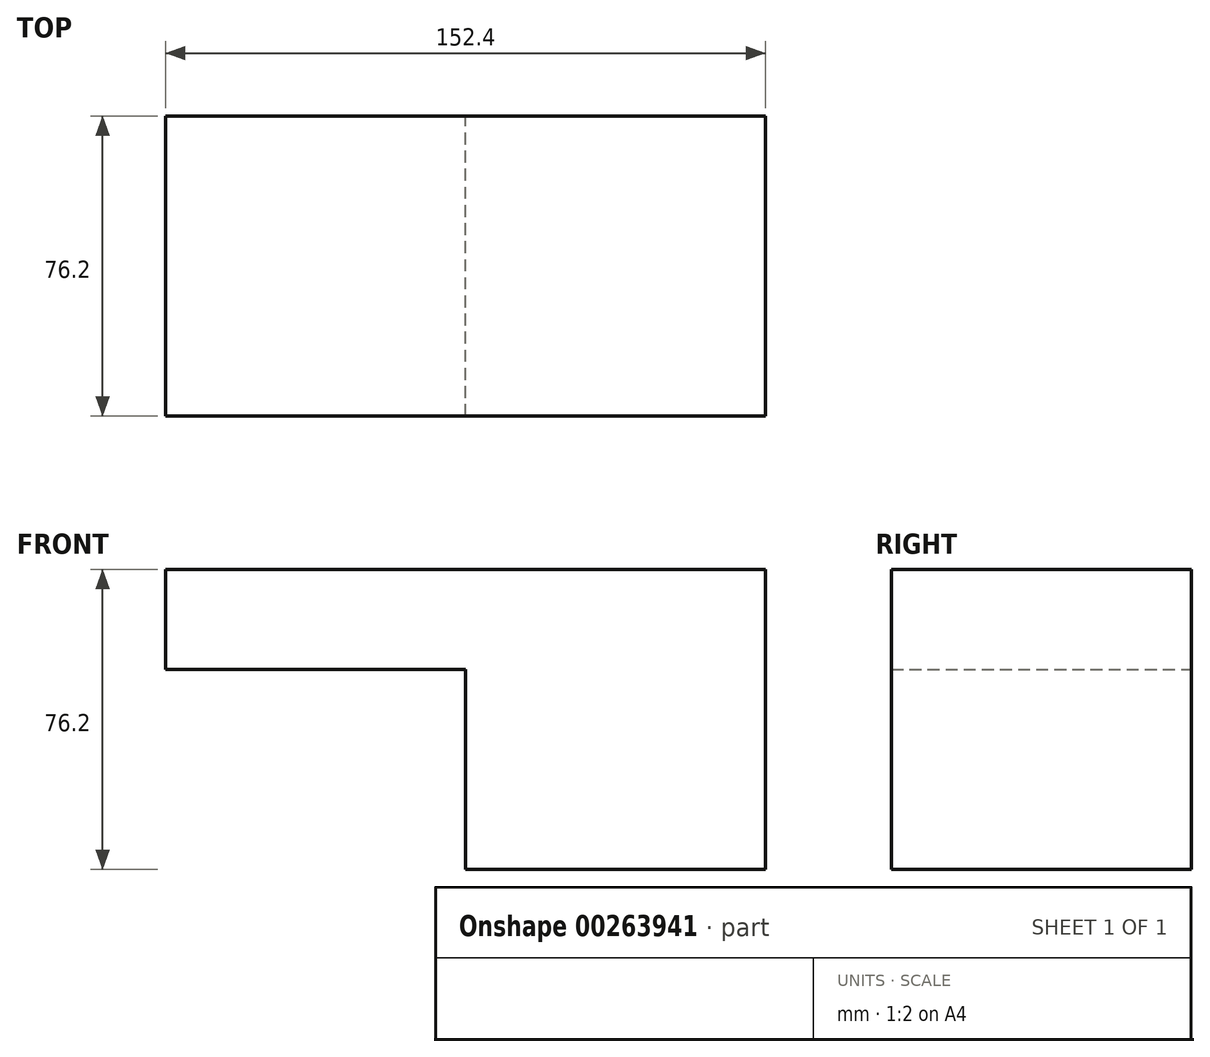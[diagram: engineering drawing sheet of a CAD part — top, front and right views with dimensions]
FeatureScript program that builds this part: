
annotation { "Feature Type Name" : "Feature", "Feature Type Description" : "" }
export const myFeature = defineFeature(function(context is Context, id is Id, definition is map)
    precondition{}
    {
        {
            var Q0;
            Q0=qCreatedBy(makeId("Top.planeOp"),FACE);
            var sketch = newSketch(context, id + "F0", { "sketchPlane" : qUnion([Q0])});
            skLineSegment(sketch, "E0.bottom", {"start": v(0, 0) * mm, "end": v(-152.4, 0) * mm});
            skLineSegment(sketch, "E0.top", {"start": v(0, 76.2) * mm, "end": v(-152.4, 76.2) * mm});
            skLineSegment(sketch, "E0.left", {"start": v(0, 0) * mm, "end": v(0, 76.2) * mm});
            skLineSegment(sketch, "E0.right", {"start": v(-152.4, 0) * mm, "end": v(-152.4, 76.2) * mm});
            skSolve(sketch);
        }
        {
            var Q0;
            Q0=makeQuery(id+"F0.imprint","IMPRINT",FACE,{"disambiguationData":[TD([[makeQuery(id+"F0.imprint","IMPRINT",EDGE,{"derivedFrom":sQuery(id+"F0.wireOp",EDGE,"E0.bottom")}),-1.0]])]});
            extrude(context, id + "F1", {"entities" : qUnion([Q0]), "depth" : 25.4 * mm});
        }
        {
            var Q0;
            Q0=qCreatedBy(makeId("Right.planeOp"),FACE);
            var sketch = newSketch(context, id + "F2", { "sketchPlane" : qUnion([Q0])});
            skLineSegment(sketch, "E1.bottom", {"start": v(0, 0) * mm, "end": v(76.2, 0) * mm});
            skLineSegment(sketch, "E1.top", {"start": v(0, -50.8) * mm, "end": v(76.2, -50.8) * mm});
            skLineSegment(sketch, "E1.left", {"start": v(0, 0) * mm, "end": v(0, -50.8) * mm});
            skLineSegment(sketch, "E1.right", {"start": v(76.2, 0) * mm, "end": v(76.2, -50.8) * mm});
            skSolve(sketch);
        }
        {
            var Q0;
            Q0=makeQuery(id+"F2.imprint","IMPRINT",FACE,{"disambiguationData":[TD([[makeQuery(id+"F2.imprint","IMPRINT",EDGE,{"derivedFrom":sQuery(id+"F2.wireOp",EDGE,"E1.bottom")}),-1.0]])]});
            extrude(context, id + "F3", {"entities" : qUnion([Q0]), "operationType" : NewBodyOperationType.ADD, "oppositeDirection" : true, "depth" : 76.2 * mm});
        }
    });
